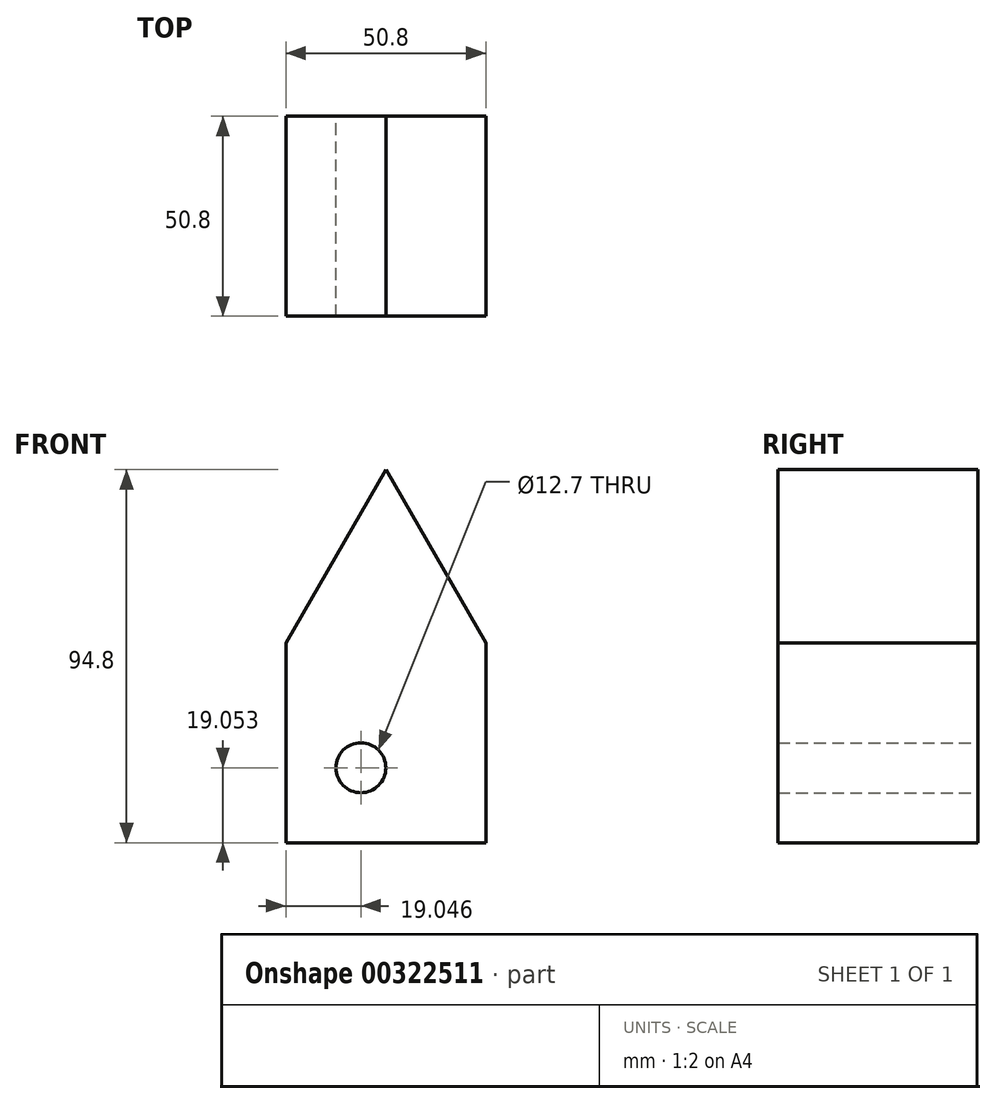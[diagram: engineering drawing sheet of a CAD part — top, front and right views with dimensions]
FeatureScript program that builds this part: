
annotation { "Feature Type Name" : "Feature", "Feature Type Description" : "" }
export const myFeature = defineFeature(function(context is Context, id is Id, definition is map)
    precondition{}
    {
        {
            var Q0;
            Q0=qCreatedBy(makeId("Front.planeOp"),FACE);
            var sketch = newSketch(context, id + "F0", { "sketchPlane" : qUnion([Q0])});
            skLineSegment(sketch, "E0.bottom", {"start": v(-10.8, 11.55) * mm, "end": v(40, 11.55) * mm});
            skLineSegment(sketch, "E0.top", {"start": v(-10.8, -39.25) * mm, "end": v(40, -39.25) * mm});
            skLineSegment(sketch, "E0.left", {"start": v(-10.8, 11.55) * mm, "end": v(-10.8, -39.25) * mm});
            skLineSegment(sketch, "E0.right", {"start": v(40, 11.55) * mm, "end": v(40, -39.25) * mm});
            skLineSegment(sketch, "E1", {"start": v(-10.8, 11.55) * mm, "end": v(14.6, 55.55) * mm});
            skLineSegment(sketch, "E2", {"start": v(14.6, 55.55) * mm, "end": v(40, 11.55) * mm});
            skLineSegment(sketch, "E3.0", {"start": v(-10.8, -20.2) * mm, "end": v(40, -20.2) * mm});
            skLineSegment(sketch, "E4.0", {"start": v(8.25, 11.55) * mm, "end": v(8.25, -39.25) * mm});
            skCircle(sketch, "E5", {"center": v(8.25, -20.2) * mm, "radius": 6.35 * mm});
            skSolve(sketch);
        }
        {
            var Q0;
            Q0 = qSketchRegion(id + "F0", true);
            extrude(context, id + "F1", {"entities" : qUnion([Q0]), "depth" : 50.8 * mm});
        }
    });
